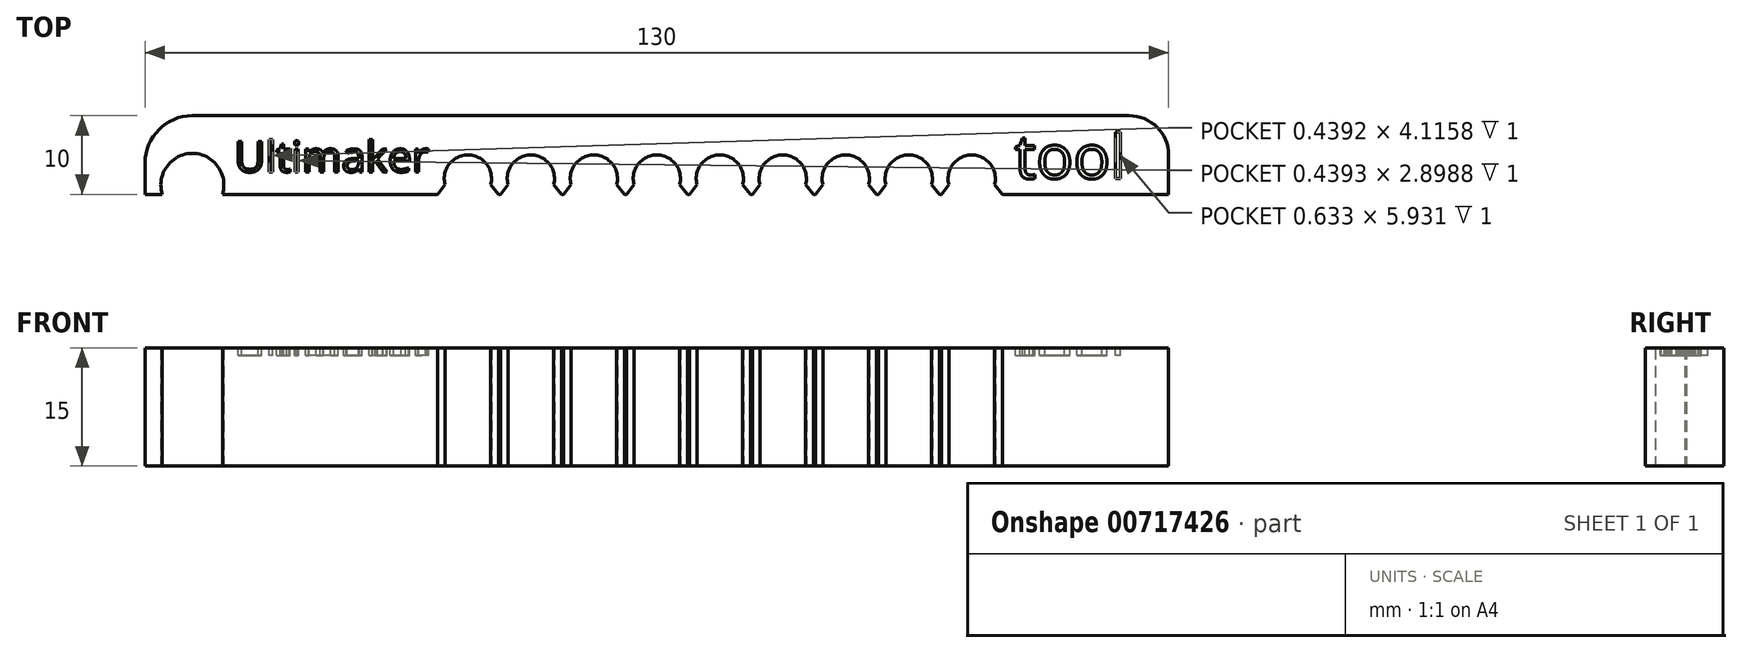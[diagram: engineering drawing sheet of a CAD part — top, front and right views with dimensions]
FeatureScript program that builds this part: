
annotation { "Feature Type Name" : "Feature", "Feature Type Description" : "" }
export const myFeature = defineFeature(function(context is Context, id is Id, definition is map)
    precondition{}
    {
        {
            var Q0;
            Q0=qCreatedBy(makeId("Top.planeOp"),FACE);
            var sketch = newSketch(context, id + "F0", { "sketchPlane" : qUnion([Q0])});
            skLineSegment(sketch, "E0", {"start": v(-16, 5) * mm, "end": v(-16, -5) * mm, "construction": true});
            skLineSegment(sketch, "E1", {"start": v(-8, -5) * mm, "end": v(-8, 5) * mm, "construction": true});
            skLineSegment(sketch, "E2", {"start": v(0, 5) * mm, "end": v(0, -5) * mm, "construction": true});
            skLineSegment(sketch, "E3", {"start": v(8, -5) * mm, "end": v(8, 5) * mm, "construction": true});
            skLineSegment(sketch, "E4", {"start": v(16, 5) * mm, "end": v(16, -5) * mm, "construction": true});
            skPoint(sketch, "E5.middle", {"position": v(0, 0) * mm});
            skLineSegment(sketch, "E6.bottom", {"start": v(-59, 5) * mm, "end": v(60, 5) * mm});
            skLineSegment(sketch, "E6.top", {"start": v(-65, -5) * mm, "end": v(65, -5) * mm});
            skLineSegment(sketch, "E6.left", {"start": v(-65, -1) * mm, "end": v(-65, -5) * mm});
            skLineSegment(sketch, "E6.right", {"start": v(65, 0) * mm, "end": v(65, -5) * mm});
            skLineSegment(sketch, "E7", {"start": v(-73.63, -3) * mm, "end": v(72.08, -3) * mm, "construction": true});
            skLineSegment(sketch, "E8", {"start": v(-59, 13.25) * mm, "end": v(-59, -5) * mm, "construction": true});
            skCircle(sketch, "E9", {"center": v(-16, -3) * mm, "radius": 3 * mm});
            skCircle(sketch, "E10", {"center": v(-8, -3) * mm, "radius": 3 * mm});
            skCircle(sketch, "E11", {"center": v(0, -3) * mm, "radius": 3 * mm});
            skCircle(sketch, "E12", {"center": v(8, -3) * mm, "radius": 3 * mm});
            skCircle(sketch, "E13", {"center": v(16, -3) * mm, "radius": 3 * mm});
            skLineSegment(sketch, "E14", {"start": v(-63, -3.8) * mm, "end": v(-55, -3.8) * mm, "construction": true});
            skCircle(sketch, "E15", {"center": v(-59, -3.8) * mm, "radius": 4 * mm});
            skLineSegment(sketch, "E16", {"start": v(-24, 5) * mm, "end": v(-24, -5) * mm, "construction": true});
            skLineSegment(sketch, "E17", {"start": v(24, 5) * mm, "end": v(24, -5) * mm, "construction": true});
            skLineSegment(sketch, "E18", {"start": v(32, 5) * mm, "end": v(32, -5) * mm, "construction": true});
            skLineSegment(sketch, "E19", {"start": v(40, 5) * mm, "end": v(40, -5) * mm, "construction": true});
            skCircle(sketch, "E20", {"center": v(-24, -3) * mm, "radius": 3 * mm});
            skCircle(sketch, "E21", {"center": v(24, -3) * mm, "radius": 3 * mm});
            skCircle(sketch, "E22", {"center": v(32, -3) * mm, "radius": 3 * mm});
            skCircle(sketch, "E23", {"center": v(40, -3) * mm, "radius": 3 * mm});
            skPoint(sketch, "E24.visualSharp", {"position": v(65, 5) * mm});
            skArc(sketch, "E24.filletArc", {"start": v(65, 0) * mm, "mid": v(63.54, 3.54) * mm, "end": v(60, 5) * mm});
            skPoint(sketch, "E25.visualSharp", {"position": v(-65, 5) * mm});
            skArc(sketch, "E25.filletArc", {"start": v(-59, 5) * mm, "mid": v(-63.24, 3.24) * mm, "end": v(-65, -1) * mm});
            skSolve(sketch);
        }
        {
            var Q0;
            Q0=makeQuery(id+"F0.imprint","IMPRINT",FACE,{"disambiguationData":[TD([[makeQuery(id+"F0.imprint","IMPRINT",EDGE,{"derivedFrom":sQuery(id+"F0.wireOp",EDGE,"E6.bottom")}),-1.0]])]});
            extrude(context, id + "F1", {"entities" : qUnion([Q0]), "depth" : 15 * mm, "offsetDistance" : 25 * mm});
        }
        {
            var Q0;
            {var subQ0=sQuery(id+"F0.wireOp",EDGE,"E20");var subQ1=sQuery(id+"F0.wireOp",EDGE,"E6.top");Q0=makeQuery(id+"F1.opExtrude","SWEPT_EDGE",EDGE,{"disambiguationData":[OSD([subQ1,subQ0]),TDD([makeQuery(id+"F0.imprint","INTERSECT",VERTEX,{"disambiguationData":[OD(1.0)],"derivedFrom":[subQ1,subQ0]})])]});}
            var Q1;
            {var subQ0=sQuery(id+"F0.wireOp",EDGE,"E9");var subQ1=sQuery(id+"F0.wireOp",EDGE,"E6.top");Q1=makeQuery(id+"F1.opExtrude","SWEPT_EDGE",EDGE,{"disambiguationData":[OSD([subQ1,subQ0]),TDD([makeQuery(id+"F0.imprint","INTERSECT",VERTEX,{"disambiguationData":[OD(1.0)],"derivedFrom":[subQ1,subQ0]})])]});}
            var Q2;
            {var subQ0=sQuery(id+"F0.wireOp",EDGE,"E10");var subQ1=sQuery(id+"F0.wireOp",EDGE,"E6.top");Q2=makeQuery(id+"F1.opExtrude","SWEPT_EDGE",EDGE,{"disambiguationData":[OSD([subQ1,subQ0]),TDD([makeQuery(id+"F0.imprint","INTERSECT",VERTEX,{"disambiguationData":[OD(1.0)],"derivedFrom":[subQ1,subQ0]})])]});}
            var Q3;
            {var subQ0=sQuery(id+"F0.wireOp",EDGE,"E20");var subQ1=sQuery(id+"F0.wireOp",EDGE,"E6.top");Q3=makeQuery(id+"F1.opExtrude","SWEPT_EDGE",EDGE,{"disambiguationData":[OSD([subQ1,subQ0]),TDD([makeQuery(id+"F0.imprint","INTERSECT",VERTEX,{"disambiguationData":[OD(0.0)],"derivedFrom":[subQ1,subQ0]})])]});}
            var Q4;
            {var subQ0=sQuery(id+"F0.wireOp",EDGE,"E9");var subQ1=sQuery(id+"F0.wireOp",EDGE,"E6.top");Q4=makeQuery(id+"F1.opExtrude","SWEPT_EDGE",EDGE,{"disambiguationData":[OSD([subQ1,subQ0]),TDD([makeQuery(id+"F0.imprint","INTERSECT",VERTEX,{"disambiguationData":[OD(0.0)],"derivedFrom":[subQ1,subQ0]})])]});}
            var Q5;
            {var subQ0=sQuery(id+"F0.wireOp",EDGE,"E10");var subQ1=sQuery(id+"F0.wireOp",EDGE,"E6.top");Q5=makeQuery(id+"F1.opExtrude","SWEPT_EDGE",EDGE,{"disambiguationData":[OSD([subQ1,subQ0]),TDD([makeQuery(id+"F0.imprint","INTERSECT",VERTEX,{"disambiguationData":[OD(0.0)],"derivedFrom":[subQ1,subQ0]})])]});}
            var Q6;
            {var subQ0=sQuery(id+"F0.wireOp",EDGE,"E11");var subQ1=sQuery(id+"F0.wireOp",EDGE,"E6.top");Q6=makeQuery(id+"F1.opExtrude","SWEPT_EDGE",EDGE,{"disambiguationData":[OSD([subQ1,subQ0]),TDD([makeQuery(id+"F0.imprint","INTERSECT",VERTEX,{"disambiguationData":[OD(0.0)],"derivedFrom":[subQ1,subQ0]})])]});}
            var Q7;
            {var subQ0=sQuery(id+"F0.wireOp",EDGE,"E12");var subQ1=sQuery(id+"F0.wireOp",EDGE,"E6.top");Q7=makeQuery(id+"F1.opExtrude","SWEPT_EDGE",EDGE,{"disambiguationData":[OSD([subQ1,subQ0]),TDD([makeQuery(id+"F0.imprint","INTERSECT",VERTEX,{"disambiguationData":[OD(0.0)],"derivedFrom":[subQ1,subQ0]})])]});}
            var Q8;
            {var subQ0=sQuery(id+"F0.wireOp",EDGE,"E11");var subQ1=sQuery(id+"F0.wireOp",EDGE,"E6.top");Q8=makeQuery(id+"F1.opExtrude","SWEPT_EDGE",EDGE,{"disambiguationData":[OSD([subQ1,subQ0]),TDD([makeQuery(id+"F0.imprint","INTERSECT",VERTEX,{"disambiguationData":[OD(1.0)],"derivedFrom":[subQ1,subQ0]})])]});}
            var Q9;
            {var subQ0=sQuery(id+"F0.wireOp",EDGE,"E21");var subQ1=sQuery(id+"F0.wireOp",EDGE,"E6.top");Q9=makeQuery(id+"F1.opExtrude","SWEPT_EDGE",EDGE,{"disambiguationData":[OSD([subQ1,subQ0]),TDD([makeQuery(id+"F0.imprint","INTERSECT",VERTEX,{"disambiguationData":[OD(0.0)],"derivedFrom":[subQ1,subQ0]})])]});}
            var Q10;
            {var subQ0=sQuery(id+"F0.wireOp",EDGE,"E13");var subQ1=sQuery(id+"F0.wireOp",EDGE,"E6.top");Q10=makeQuery(id+"F1.opExtrude","SWEPT_EDGE",EDGE,{"disambiguationData":[OSD([subQ1,subQ0]),TDD([makeQuery(id+"F0.imprint","INTERSECT",VERTEX,{"disambiguationData":[OD(0.0)],"derivedFrom":[subQ1,subQ0]})])]});}
            var Q11;
            {var subQ0=sQuery(id+"F0.wireOp",EDGE,"E12");var subQ1=sQuery(id+"F0.wireOp",EDGE,"E6.top");Q11=makeQuery(id+"F1.opExtrude","SWEPT_EDGE",EDGE,{"disambiguationData":[OSD([subQ1,subQ0]),TDD([makeQuery(id+"F0.imprint","INTERSECT",VERTEX,{"disambiguationData":[OD(1.0)],"derivedFrom":[subQ1,subQ0]})])]});}
            var Q12;
            {var subQ0=sQuery(id+"F0.wireOp",EDGE,"E13");var subQ1=sQuery(id+"F0.wireOp",EDGE,"E6.top");Q12=makeQuery(id+"F1.opExtrude","SWEPT_EDGE",EDGE,{"disambiguationData":[OSD([subQ1,subQ0]),TDD([makeQuery(id+"F0.imprint","INTERSECT",VERTEX,{"disambiguationData":[OD(1.0)],"derivedFrom":[subQ1,subQ0]})])]});}
            var Q13;
            {var subQ0=sQuery(id+"F0.wireOp",EDGE,"E23");var subQ1=sQuery(id+"F0.wireOp",EDGE,"E6.top");Q13=makeQuery(id+"F1.opExtrude","SWEPT_EDGE",EDGE,{"disambiguationData":[OSD([subQ1,subQ0]),TDD([makeQuery(id+"F0.imprint","INTERSECT",VERTEX,{"disambiguationData":[OD(0.0)],"derivedFrom":[subQ1,subQ0]})])]});}
            var Q14;
            {var subQ0=sQuery(id+"F0.wireOp",EDGE,"E22");var subQ1=sQuery(id+"F0.wireOp",EDGE,"E6.top");Q14=makeQuery(id+"F1.opExtrude","SWEPT_EDGE",EDGE,{"disambiguationData":[OSD([subQ1,subQ0]),TDD([makeQuery(id+"F0.imprint","INTERSECT",VERTEX,{"disambiguationData":[OD(1.0)],"derivedFrom":[subQ1,subQ0]})])]});}
            var Q15;
            {var subQ0=sQuery(id+"F0.wireOp",EDGE,"E22");var subQ1=sQuery(id+"F0.wireOp",EDGE,"E6.top");Q15=makeQuery(id+"F1.opExtrude","SWEPT_EDGE",EDGE,{"disambiguationData":[OSD([subQ1,subQ0]),TDD([makeQuery(id+"F0.imprint","INTERSECT",VERTEX,{"disambiguationData":[OD(0.0)],"derivedFrom":[subQ1,subQ0]})])]});}
            var Q16;
            {var subQ0=sQuery(id+"F0.wireOp",EDGE,"E21");var subQ1=sQuery(id+"F0.wireOp",EDGE,"E6.top");Q16=makeQuery(id+"F1.opExtrude","SWEPT_EDGE",EDGE,{"disambiguationData":[OSD([subQ1,subQ0]),TDD([makeQuery(id+"F0.imprint","INTERSECT",VERTEX,{"disambiguationData":[OD(1.0)],"derivedFrom":[subQ1,subQ0]})])]});}
            var Q17;
            {var subQ0=sQuery(id+"F0.wireOp",EDGE,"E23");var subQ1=sQuery(id+"F0.wireOp",EDGE,"E6.top");Q17=makeQuery(id+"F1.opExtrude","SWEPT_EDGE",EDGE,{"disambiguationData":[OSD([subQ1,subQ0]),TDD([makeQuery(id+"F0.imprint","INTERSECT",VERTEX,{"disambiguationData":[OD(1.0)],"derivedFrom":[subQ1,subQ0]})])]});}
            chamfer(context, id + "F2", {"entities" : qUnion([Q0, Q1, Q2, Q3, Q4, Q5, Q6, Q7, Q8, Q9, Q10, Q11, Q12, Q13, Q14, Q15, Q16, Q17]), "width" : 1 * mm, "tangentPropagation" : true});
        }
        {
            var Q0;
            Q0=makeQuery(id+"F1.opExtrude","CAP_FACE",FACE,{"disambiguationData":[OSD([sQuery(id+"F0.wireOp",EDGE,"E6.bottom"),sQuery(id+"F0.wireOp",EDGE,"E6.top"),sQuery(id+"F0.wireOp",EDGE,"E6.left"),sQuery(id+"F0.wireOp",EDGE,"E6.right"),sQuery(id+"F0.wireOp",EDGE,"E9"),sQuery(id+"F0.wireOp",EDGE,"E10"),sQuery(id+"F0.wireOp",EDGE,"E11"),sQuery(id+"F0.wireOp",EDGE,"E12"),sQuery(id+"F0.wireOp",EDGE,"E13"),sQuery(id+"F0.wireOp",EDGE,"E15"),sQuery(id+"F0.wireOp",EDGE,"E20"),sQuery(id+"F0.wireOp",EDGE,"E21"),sQuery(id+"F0.wireOp",EDGE,"E22"),sQuery(id+"F0.wireOp",EDGE,"E23"),sQuery(id+"F0.wireOp",EDGE,"E24.filletArc"),sQuery(id+"F0.wireOp",EDGE,"E25.filletArc")])],"isStart":false});
            var sketch = newSketch(context, id + "F3", { "sketchPlane" : qUnion([Q0])});
            skText(sketch, "E26", { "text": "Ultimaker", "fontName": "OpenSans-Regular.ttf"});
            skText(sketch, "E27", { "text": "tool", "fontName": "OpenSans-Regular.ttf"});
            const initialGuessF3  = {"E26": [-0.05367, -0.00216, 1, 0, 0.0039], "E27": [0.04543, -0.003, 1, 0, 0.00562]};
            skSetInitialGuess(sketch, initialGuessF3);
            skSolve(sketch);
        }
        {
            var Q0;
            Q0 = qSketchRegion(id + "F3", true);
            extrude(context, id + "F4", {"entities" : qUnion([Q0]), "operationType" : NewBodyOperationType.REMOVE, "oppositeDirection" : true, "depth" : 1 * mm, "offsetDistance" : 25 * mm});
        }
    });
